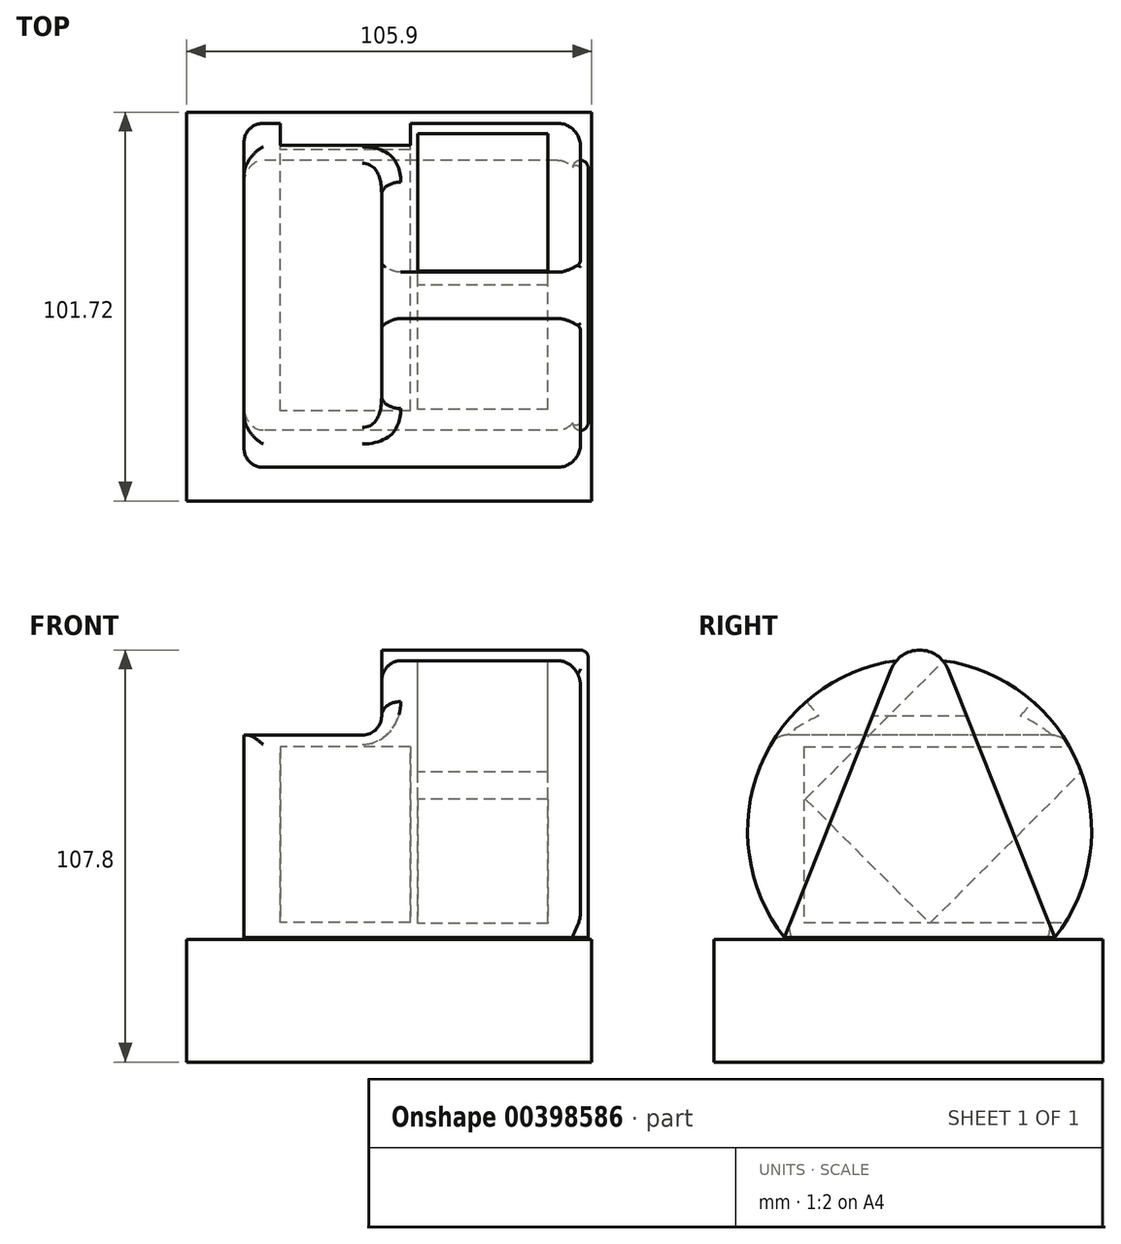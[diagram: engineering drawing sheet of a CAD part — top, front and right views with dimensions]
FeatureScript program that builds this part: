
annotation { "Feature Type Name" : "Feature", "Feature Type Description" : "" }
export const myFeature = defineFeature(function(context is Context, id is Id, definition is map)
    precondition{}
    {
        {
            var Q0;
            Q0=qCreatedBy(makeId("Right.planeOp"),FACE);
            var sketch = newSketch(context, id + "F0", { "sketchPlane" : qUnion([Q0])});
            skLineSegment(sketch, "E0.bottom", {"start": v(-143.02, 37.92) * mm, "end": v(56.98, 37.92) * mm});
            skLineSegment(sketch, "E0.top", {"start": v(-143.02, -7.08) * mm, "end": v(56.98, -7.08) * mm});
            skLineSegment(sketch, "E0.left", {"start": v(-143.02, 37.92) * mm, "end": v(-143.02, -7.08) * mm});
            skLineSegment(sketch, "E0.right", {"start": v(56.98, 37.92) * mm, "end": v(56.98, -7.08) * mm});
            skSolve(sketch);
        }
        {
            var Q0;
            Q0 = qSketchRegion(id + "F0", true);
            extrude(context, id + "F1", {"entities" : qUnion([Q0]), "depth" : 33 * mm});
        }
        {
            var Q0;
            Q0=makeQuery(id+"F1.opExtrude","SWEPT_BODY",BODY,{"disambiguationData":[OSD([sQuery(id+"F0.wireOp",EDGE,"E0.bottom"),sQuery(id+"F0.wireOp",EDGE,"E0.top"),sQuery(id+"F0.wireOp",EDGE,"E0.left"),sQuery(id+"F0.wireOp",EDGE,"E0.right")])]});
            var Q1;
            Q1=makeQuery(id+"F1.opExtrude","SWEPT_EDGE",EDGE,{"disambiguationData":[OSD([sQuery(id+"F0.wireOp",EDGE,"E0.top"),sQuery(id+"F0.wireOp",EDGE,"E0.left")])]});
            transform(context, id + "F2", {"entities" : qUnion([Q0]), "transformType" : TransformType.ROTATION, "transformAxis" : qUnion([Q1]), "angle" : 45 * degree, "oppositeDirection" : true, "makeCopy" : true});
        }
        {
            var Q0;
            Q0=makeQuery(id+"F2.opPattern","COPY",BODY,{"derivedFrom":makeQuery(id+"F1.opExtrude","SWEPT_BODY",BODY,{"disambiguationData":[OSD([sQuery(id+"F0.wireOp",EDGE,"E0.bottom"),sQuery(id+"F0.wireOp",EDGE,"E0.top"),sQuery(id+"F0.wireOp",EDGE,"E0.left"),sQuery(id+"F0.wireOp",EDGE,"E0.right")])]}),"instanceName":"1"});
            transform(context, id + "F3", {"entities" : qUnion([Q0]), "transformType" : TransformType.TRANSLATION_3D, "dx" : 36 * mm, "dy" : 32.4 * mm, "dz" : 0 * mm, "makeCopy" : false});
        }
        {
            var Q0;
            Q0=qCreatedBy(makeId("Right.planeOp"),FACE);
            var sketch = newSketch(context, id + "F4", { "sketchPlane" : qUnion([Q0])});
            skCircle(sketch, "E1", {"center": v(-113.27, 16.38) * mm, "radius": 45 * mm});
            skSolve(sketch);
        }
        {
            var Q0;
            Q0 = qSketchRegion(id + "F4", true);
            extrude(context, id + "F5", {"entities" : qUnion([Q0]), "depth" : 88 * mm});
        }
        {
            var Q0;
            Q0=makeQuery(id+"F5.opExtrude","SWEPT_BODY",BODY,{"disambiguationData":[OSD([sQuery(id+"F4.wireOp",EDGE,"E1")])]});
            transform(context, id + "F6", {"entities" : qUnion([Q0]), "transformType" : TransformType.TRANSLATION_3D, "dx" : -10 * mm, "dy" : 0 * mm, "dz" : 0 * mm, "makeCopy" : false});
        }
        {
            var Q0;
            Q0=qCreatedBy(makeId("Right.planeOp"),FACE);
            var sketch = newSketch(context, id + "F7", { "sketchPlane" : qUnion([Q0])});
            skLineSegment(sketch, "E2.bottom", {"start": v(-167.08, -11.95) * mm, "end": v(-65.36, -11.95) * mm});
            skLineSegment(sketch, "E2.top", {"start": v(-167.08, -44.07) * mm, "end": v(-65.36, -44.07) * mm});
            skLineSegment(sketch, "E2.left", {"start": v(-167.08, -11.95) * mm, "end": v(-167.08, -44.07) * mm});
            skLineSegment(sketch, "E2.right", {"start": v(-65.36, -11.95) * mm, "end": v(-65.36, -44.07) * mm});
            skLineSegment(sketch, "E3", {"start": v(-74.71, -11.95) * mm, "end": v(-74.71, -6.95) * mm});
            skLineSegment(sketch, "E4", {"start": v(-74.71, -6.95) * mm, "end": v(-35.59, -6.95) * mm});
            skSolve(sketch);
        }
        {
            var Q0;
            Q0=makeQuery(id+"F7.imprint","IMPRINT",FACE,{"disambiguationData":[TD([[makeQuery(id+"F7.imprint","IMPRINT",EDGE,{"derivedFrom":sQuery(id+"F7.wireOp",EDGE,"E2.top")}),1.0]])]});
            extrude(context, id + "F8", {"entities" : qUnion([Q0]), "depth" : 80.9 * mm, "hasSecondDirection" : true, "secondDirectionOppositeDirection" : true, "secondDirectionDepth" : 25 * mm});
        }
        {
            var Q0;
            Q0=makeQuery(id+"F8.opExtrude","SWEPT_BODY",BODY,{"disambiguationData":[OSD([sQuery(id+"F7.wireOp",EDGE,"E2.bottom"),sQuery(id+"F7.wireOp",EDGE,"E2.top"),sQuery(id+"F7.wireOp",EDGE,"E2.left"),sQuery(id+"F7.wireOp",EDGE,"E2.right")])]});
            var Q1;
            Q1=makeQuery(id+"F5.opExtrude","SWEPT_BODY",BODY,{"disambiguationData":[OSD([sQuery(id+"F4.wireOp",EDGE,"E1")])]});
            booleanBodies(context, id + "F9", {"operationType" : BooleanOperationType.SUBTRACTION, "tools" : qUnion([Q0]), "targets" : qUnion([Q1]), "offset" : true, "offsetAll" : true, "offsetDistance" : .5 * mm, "keepTools" : true});
        }
        {
            var Q0;
            Q0=makeQuery(id+"F5.opExtrude","CAP_FACE",FACE,{"disambiguationData":[OSD([sQuery(id+"F4.wireOp",EDGE,"E1")])],"isStart":false});
            var sketch = newSketch(context, id + "F10", { "sketchPlane" : qUnion([Q0])});
            skLineSegment(sketch, "E5", {"start": v(-148.64, -11.45) * mm, "end": v(-120.7, 58.69) * mm});
            skPoint(sketch, "E5.endSnap0", {"position": v(-113.27, 61.38) * mm});
            skLineSegment(sketch, "E6", {"start": v(-105.84, 58.69) * mm, "end": v(-77.91, -11.45) * mm});
            skLineSegment(sketch, "E7", {"start": v(-77.91, -11.45) * mm, "end": v(-148.64, -11.45) * mm});
            skPoint(sketch, "E8.visualSharp", {"position": v(-113.27, 77.35) * mm});
            skArc(sketch, "E8.filletArc", {"start": v(-105.84, 58.69) * mm, "mid": v(-113.27, 63.73) * mm, "end": v(-120.7, 58.69) * mm});
            skSolve(sketch);
        }
        {
            var Q0;
            Q0 = qSketchRegion(id + "F10", true);
            extrude(context, id + "F11", {"entities" : qUnion([Q0]), "depth" : 2 * mm, "hasSecondDirection" : true, "secondDirectionOppositeDirection" : true, "secondDirectionDepth" : 56 * mm});
        }
        {
            var Q0;
            Q0=makeQuery(id+"F11.opExtrude","CAP_EDGE",EDGE,{"disambiguationData":[OSD([sQuery(id+"F10.wireOp",EDGE,"E8.filletArc")])],"isStart":true});
            fillet(context, id + "F12", {"entities" : qUnion([Q0]), "radius" : 3.86 * mm, "tangentPropagation" : true, "allowEdgeOverflow" : false});
        }
        {
            var Q0;
            Q0=makeQuery(id+"F11.opExtrude","CAP_EDGE",EDGE,{"disambiguationData":[OSD([sQuery(id+"F10.wireOp",EDGE,"E6")])],"isStart":false});
            var Q1;
            Q1=makeQuery(id+"F11.opExtrude","CAP_EDGE",EDGE,{"disambiguationData":[OSD([sQuery(id+"F10.wireOp",EDGE,"E8.filletArc")])],"isStart":false});
            var Q2;
            Q2=makeQuery(id+"F11.opExtrude","CAP_EDGE",EDGE,{"disambiguationData":[OSD([sQuery(id+"F10.wireOp",EDGE,"E5")])],"isStart":false});
            fillet(context, id + "F13", {"entities" : qUnion([Q0, Q1, Q2]), "radius" : 2 * mm, "tangentPropagation" : true, "allowEdgeOverflow" : false});
        }
        {
            var Q0;
            Q0=makeQuery(id+"F5.opExtrude","CAP_FACE",FACE,{"disambiguationData":[OSD([sQuery(id+"F4.wireOp",EDGE,"E1")])],"isStart":true});
            var sketch = newSketch(context, id + "F14", { "sketchPlane" : qUnion([Q0])});
            skLineSegment(sketch, "E9.bottom", {"start": v(75.93, 41.5) * mm, "end": v(165.93, 41.5) * mm});
            skLineSegment(sketch, "E9.top", {"start": v(75.93, 81.5) * mm, "end": v(165.93, 81.5) * mm});
            skLineSegment(sketch, "E9.left", {"start": v(75.93, 41.5) * mm, "end": v(75.93, 81.5) * mm});
            skLineSegment(sketch, "E9.right", {"start": v(165.93, 41.5) * mm, "end": v(165.93, 81.5) * mm});
            skSolve(sketch);
        }
        {
            var Q0;
            Q0 = qSketchRegion(id + "F14", true);
            extrude(context, id + "F15", {"entities" : qUnion([Q0]), "operationType" : NewBodyOperationType.REMOVE, "oppositeDirection" : true, "depth" : 36 * mm});
        }
        {
            var Q0;
            Q0=makeQuery(id+"F15.boolean.opBoolean","COPY",EDGE,{"derivedFrom":makeQuery(id+"F15.opExtrude","CAP_EDGE",EDGE,{"disambiguationData":[OSD([sQuery(id+"F14.wireOp",EDGE,"E9.bottom")])],"isStart":true})});
            var Q1;
            Q1=makeQuery(id+"F15.boolean.opBoolean","COPY",EDGE,{"derivedFrom":makeQuery(id+"F15.opExtrude","CAP_EDGE",EDGE,{"disambiguationData":[OSD([sQuery(id+"F14.wireOp",EDGE,"E9.bottom")])],"isStart":false})});
            var Q2;
            Q2=makeQuery(id+"F15.boolean.opBoolean","INTERSECT",EDGE,{"derivedFrom":[makeQuery(id+"F5.opExtrude","SWEPT_FACE",FACE,{"disambiguationData":[OSD([sQuery(id+"F4.wireOp",EDGE,"E1")])]}),makeQuery(id+"F15.opExtrude","CAP_FACE",FACE,{"disambiguationData":[OSD([sQuery(id+"F14.wireOp",EDGE,"E9.bottom"),sQuery(id+"F14.wireOp",EDGE,"E9.top"),sQuery(id+"F14.wireOp",EDGE,"E9.left"),sQuery(id+"F14.wireOp",EDGE,"E9.right")])],"isStart":false})]});
            var Q3;
            Q3=makeQuery(id+"F15.boolean.opBoolean","SPLIT",EDGE,{"disambiguationData":[OD(0.0)],"derivedFrom":makeQuery(id+"F5.opExtrude","CAP_EDGE",EDGE,{"disambiguationData":[OSD([sQuery(id+"F4.wireOp",EDGE,"E1")])],"isStart":true})});
            var Q4;
            Q4=makeQuery(id+"F15.boolean.opBoolean","SPLIT",EDGE,{"disambiguationData":[OD(1.0)],"derivedFrom":makeQuery(id+"F5.opExtrude","CAP_EDGE",EDGE,{"disambiguationData":[OSD([sQuery(id+"F4.wireOp",EDGE,"E1")])],"isStart":true})});
            var Q5;
            Q5=makeQuery(id+"F15.boolean.opBoolean","INTERSECT",EDGE,{"derivedFrom":[makeQuery(id+"F5.opExtrude","SWEPT_FACE",FACE,{"disambiguationData":[OSD([sQuery(id+"F4.wireOp",EDGE,"E1")])]}),makeQuery(id+"F15.opExtrude","SWEPT_FACE",FACE,{"disambiguationData":[OSD([sQuery(id+"F14.wireOp",EDGE,"E9.bottom")])]})]});
            fillet(context, id + "F16", {"entities" : qUnion([Q0, Q1, Q2, Q3, Q4, Q5]), "radius" : 5 * mm, "tangentPropagation" : true, "allowEdgeOverflow" : false});
        }
        {
            var Q0;
            Q0=makeQuery(id+"F11.opExtrude","SWEPT_BODY",BODY,{"disambiguationData":[OSD([sQuery(id+"F10.wireOp",EDGE,"E5"),sQuery(id+"F10.wireOp",EDGE,"E6"),sQuery(id+"F10.wireOp",EDGE,"E7"),sQuery(id+"F10.wireOp",EDGE,"E8.filletArc")])]});
            var Q1;
            Q1=makeQuery(id+"F5.opExtrude","SWEPT_BODY",BODY,{"disambiguationData":[OSD([sQuery(id+"F4.wireOp",EDGE,"E1")])]});
            booleanBodies(context, id + "F17", {"operationType" : BooleanOperationType.UNION, "tools" : qUnion([Q0, Q1])});
        }
        {
            var Q0;
            Q0=makeQuery(id+"F2.opPattern","COPY",BODY,{"derivedFrom":makeQuery(id+"F1.opExtrude","SWEPT_BODY",BODY,{"disambiguationData":[OSD([sQuery(id+"F0.wireOp",EDGE,"E0.bottom"),sQuery(id+"F0.wireOp",EDGE,"E0.top"),sQuery(id+"F0.wireOp",EDGE,"E0.left"),sQuery(id+"F0.wireOp",EDGE,"E0.right")])]}),"instanceName":"1"});
            var Q1;
            Q1=makeQuery(id+"F1.opExtrude","SWEPT_BODY",BODY,{"disambiguationData":[OSD([sQuery(id+"F0.wireOp",EDGE,"E0.bottom"),sQuery(id+"F0.wireOp",EDGE,"E0.top"),sQuery(id+"F0.wireOp",EDGE,"E0.left"),sQuery(id+"F0.wireOp",EDGE,"E0.right")])]});
            var Q2;
            Q2=makeQuery(id+"F11.opExtrude","SWEPT_BODY",BODY,{"disambiguationData":[OSD([sQuery(id+"F10.wireOp",EDGE,"E5"),sQuery(id+"F10.wireOp",EDGE,"E6"),sQuery(id+"F10.wireOp",EDGE,"E7"),sQuery(id+"F10.wireOp",EDGE,"E8.filletArc")])]});
            booleanBodies(context, id + "F18", {"operationType" : BooleanOperationType.SUBTRACTION, "tools" : qUnion([Q0, Q1]), "targets" : qUnion([Q2]), "offset" : true, "offsetAll" : true, "offsetDistance" : .5 * mm});
        }
        {
            var Q0;
            {var subQ0=sQuery(id+"F4.wireOp",EDGE,"E1");Q0=makeQuery(id+"F17.opBoolean","SPLIT",EDGE,{"disambiguationData":[TD([makeQuery(id+"F13.opFillet","BLEND_FACE",FACE,{"disambiguationData":[OSD([sQuery(id+"F10.wireOp",EDGE,"E5")])]})])],"derivedFrom":makeQuery(id+"F5.opExtrude","CAP_EDGE",EDGE,{"disambiguationData":[OSD([subQ0])],"isStart":false})});}
            var Q1;
            {var subQ0=sQuery(id+"F4.wireOp",EDGE,"E1");Q1=makeQuery(id+"F17.opBoolean","SPLIT",EDGE,{"disambiguationData":[TD([makeQuery(id+"F13.opFillet","BLEND_FACE",FACE,{"disambiguationData":[OSD([sQuery(id+"F10.wireOp",EDGE,"E6")])]})])],"derivedFrom":makeQuery(id+"F5.opExtrude","CAP_EDGE",EDGE,{"disambiguationData":[OSD([subQ0])],"isStart":false})});}
            fillet(context, id + "F19", {"entities" : qUnion([Q0, Q1]), "radius" : 6 * mm, "tangentPropagation" : true, "allowEdgeOverflow" : false});
        }
    });
